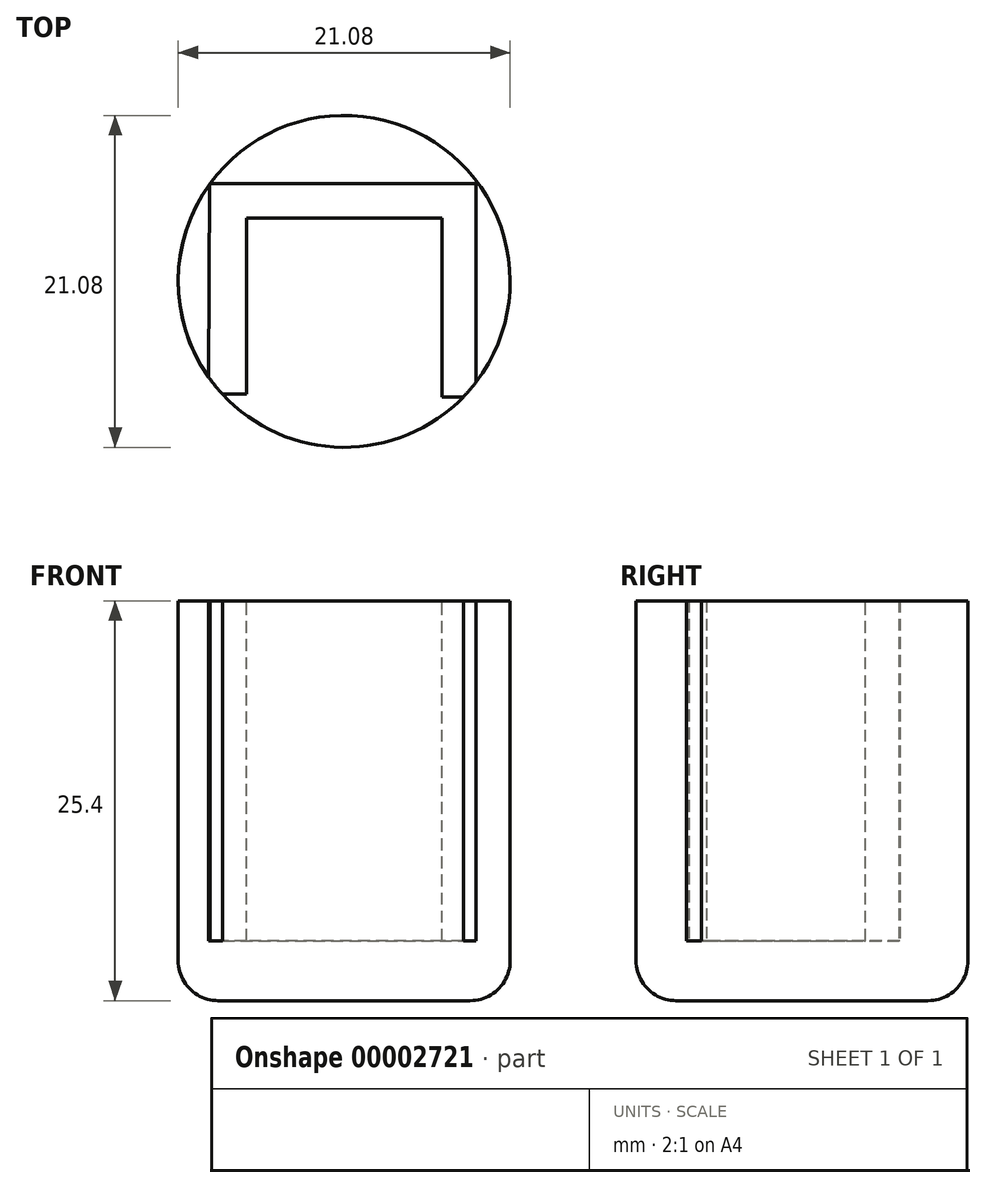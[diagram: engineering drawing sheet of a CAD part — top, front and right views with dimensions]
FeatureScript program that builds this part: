
annotation { "Feature Type Name" : "Feature", "Feature Type Description" : "" }
export const myFeature = defineFeature(function(context is Context, id is Id, definition is map)
    precondition{}
    {
        {
            var Q0;
            Q0=qCreatedBy(makeId("Top.planeOp"),FACE);
            cPlane(context, id + "F0", {"entities" : qUnion([Q0]), "cplaneType" : CPlaneType.OFFSET, "offset" : 25.4 * mm, "width" : 152.4 * mm, "height" : 152.4 * mm});
        }
        {
            var Q0;
            Q0=qCreatedBy(makeId("Top.planeOp"),FACE);
            var sketch = newSketch(context, id + "F1", { "sketchPlane" : qUnion([Q0])});
            skCircle(sketch, "E0", {"center": v(0, -6.22) * mm, "radius": 10.54 * mm});
            skSolve(sketch);
        }
        {
            var Q0;
            Q0=makeQuery(id+"F1.imprint","IMPRINT",FACE,{"disambiguationData":[TD([[makeQuery(id+"F1.imprint","IMPRINT",EDGE,{"derivedFrom":sQuery(id+"F1.wireOp",EDGE,"E0")}),1.0]])]});
            extrude(context, id + "F2", {"entities" : qUnion([Q0]), "depth" : 25.4 * mm});
        }
        {
            var Q0;
            Q0=qCreatedBy(id+"F0.planeOp",FACE);
            var sketch = newSketch(context, id + "F3", { "sketchPlane" : qUnion([Q0])});
            skLineSegment(sketch, "E1", {"start": v(-8.56, 0) * mm, "end": v(8.38, 0) * mm});
            skLineSegment(sketch, "E2", {"start": v(8.38, 0) * mm, "end": v(8.38, -13.56) * mm});
            skLineSegment(sketch, "E3", {"start": v(8.38, -13.56) * mm, "end": v(6.23, -13.56) * mm});
            skLineSegment(sketch, "E4", {"start": v(6.23, -13.56) * mm, "end": v(6.23, -2.2) * mm});
            skLineSegment(sketch, "E5", {"start": v(6.23, -2.2) * mm, "end": v(-6.2, -2.2) * mm});
            skLineSegment(sketch, "E6", {"start": v(-6.2, -2.2) * mm, "end": v(-6.2, -13.4) * mm});
            skLineSegment(sketch, "E7", {"start": v(-6.2, -13.4) * mm, "end": v(-8.62, -13.4) * mm});
            skLineSegment(sketch, "E8", {"start": v(-8.62, -13.4) * mm, "end": v(-8.56, 0) * mm});
            skSolve(sketch);
        }
        {
            var Q0;
            Q0=makeQuery(id+"F3.imprint","IMPRINT",FACE,{"disambiguationData":[TD([[makeQuery(id+"F3.imprint","IMPRINT",EDGE,{"derivedFrom":sQuery(id+"F3.wireOp",EDGE,"E1")}),-1.0]])]});
            extrude(context, id + "F4", {"entities" : qUnion([Q0]), "operationType" : NewBodyOperationType.REMOVE, "oppositeDirection" : true, "depth" : 21.59 * mm});
        }
        {
            var Q0;
            Q0=makeQuery(id+"F2.opExtrude","CAP_EDGE",EDGE,{"disambiguationData":[OSD([sQuery(id+"F1.wireOp",EDGE,"E0")])],"isStart":true});
            fillet(context, id + "F5", {"entities" : qUnion([Q0]), "radius" : 2.54 * mm, "tangentPropagation" : true, "allowEdgeOverflow" : false});
        }
    });
